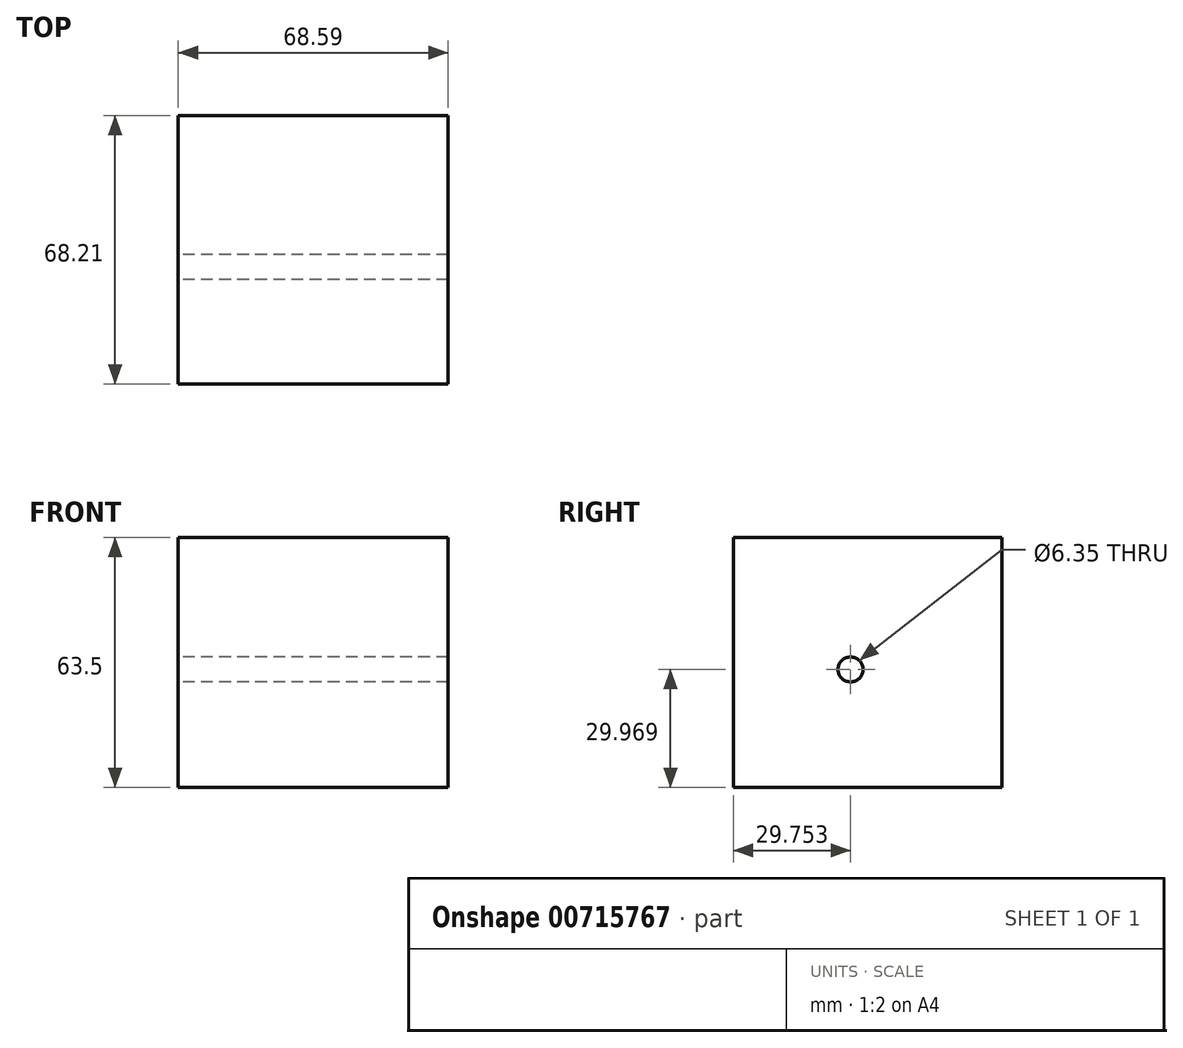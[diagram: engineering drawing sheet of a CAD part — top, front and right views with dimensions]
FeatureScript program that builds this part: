
annotation { "Feature Type Name" : "Feature", "Feature Type Description" : "" }
export const myFeature = defineFeature(function(context is Context, id is Id, definition is map)
    precondition{}
    {
        {
            var Q0;
            Q0=qCreatedBy(makeId("Top.planeOp"),FACE);
            var sketch = newSketch(context, id + "F0", { "sketchPlane" : qUnion([Q0])});
            skLineSegment(sketch, "E0.bottom", {"start": v(0, 0) * mm, "end": v(-68.59, 0) * mm});
            skLineSegment(sketch, "E0.top", {"start": v(0, 68.2) * mm, "end": v(-68.59, 68.2) * mm});
            skLineSegment(sketch, "E0.left", {"start": v(0, 0) * mm, "end": v(0, 68.2) * mm});
            skLineSegment(sketch, "E0.right", {"start": v(-68.59, 0) * mm, "end": v(-68.59, 68.2) * mm});
            skSolve(sketch);
        }
        {
            var Q0;
            Q0 = qSketchRegion(id + "F0", true);
            extrude(context, id + "F1", {"entities" : qUnion([Q0]), "depth" : 63.5 * mm, "offsetDistance" : 25.4 * mm});
        }
        {
            var Q0;
            Q0=makeQuery(id+"F1.opExtrude","SWEPT_FACE",FACE,{"disambiguationData":[OSD([sQuery(id+"F0.wireOp",EDGE,"E0.right")])]});
            var sketch = newSketch(context, id + "F2", { "sketchPlane" : qUnion([Q0])});
            skCircle(sketch, "E1", {"center": v(-29.75, 29.97) * mm, "radius": 12.64 * mm});
            skSolve(sketch);
        }
        {
            var Q0;
            Q0=sQuery(id+"F2.wireOp",VERTEX,"E1.center");
            var Q1;
            Q1=makeQuery(id+"F1.opExtrude","SWEPT_BODY",BODY,{"disambiguationData":[OSD([sQuery(id+"F0.wireOp",EDGE,"E0.bottom"),sQuery(id+"F0.wireOp",EDGE,"E0.top"),sQuery(id+"F0.wireOp",EDGE,"E0.left"),sQuery(id+"F0.wireOp",EDGE,"E0.right")])]});
            hole(context, id + "F3", {"style" : HoleStyle.SIMPLE, "endStyle" : HoleEndStyle.THROUGH, "holeDiameter" : 6.35 * mm, "majorDiameter" : 6.35 * mm, "isTappedThrough" : true, "tappedDepth" : 12.7 * mm, "tapClearance" : 3, "locations" : qUnion([Q0]), "scope" : qUnion([Q1])});
        }
    });
